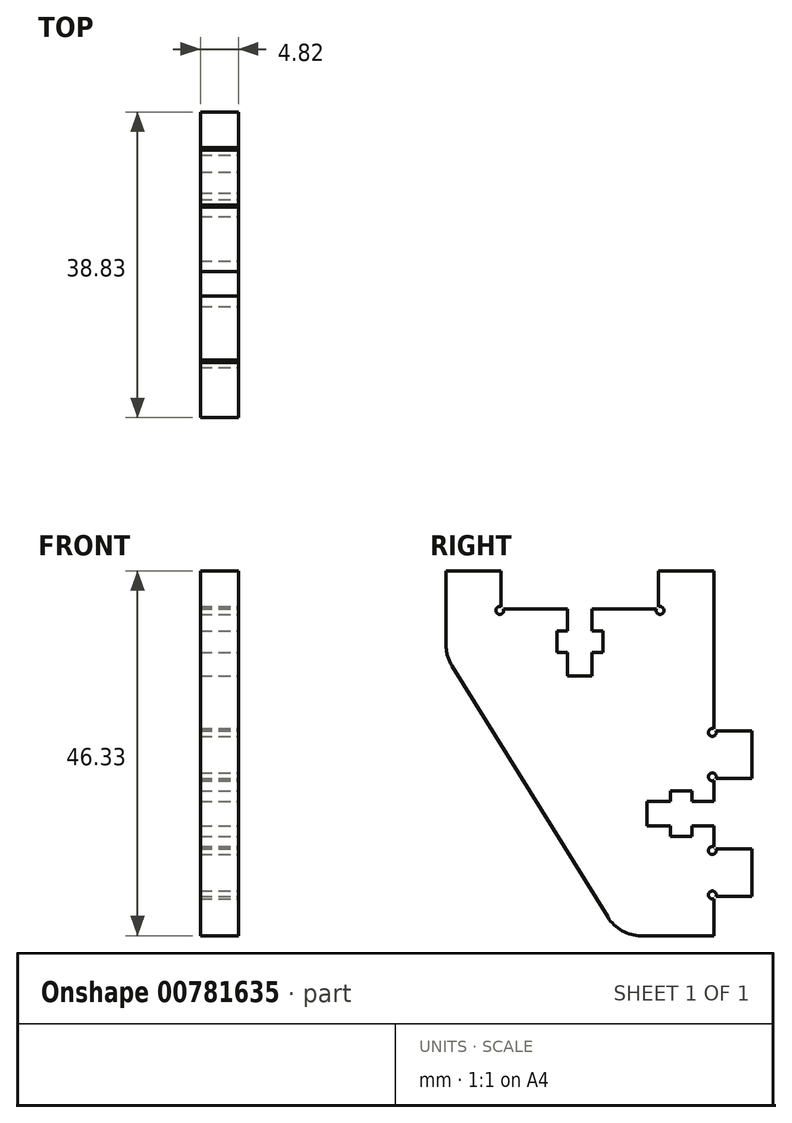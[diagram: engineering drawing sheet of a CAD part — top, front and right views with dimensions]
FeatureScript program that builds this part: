
annotation { "Feature Type Name" : "Feature", "Feature Type Description" : "" }
export const myFeature = defineFeature(function(context is Context, id is Id, definition is map)
    precondition{}
    {
        {
            var Q0;
            Q0=qCreatedBy(makeId("Right.planeOp"),FACE);
            var sketch = newSketch(context, id + "F0", { "sketchPlane" : qUnion([Q0])});
            skLineSegment(sketch, "E0.top", {"start": v(17, 0) * mm, "end": v(-17, 0) * mm});
            skLineSegment(sketch, "E0.left", {"start": v(17, -41.5) * mm, "end": v(17, 0) * mm});
            skLineSegment(sketch, "E0.right", {"start": v(-17, -6) * mm, "end": v(-17, 0) * mm});
            skPoint(sketch, "E0.middle", {"position": v(0, 0) * mm});
            skLineSegment(sketch, "E1", {"start": v(5, -41.5) * mm, "end": v(17, -41.5) * mm});
            skLineSegment(sketch, "E2", {"start": v(-17, -6) * mm, "end": v(5, -41.5) * mm});
            skSolve(sketch);
        }
        {
            var Q0;
            Q0=qSketchRegion(id+"F0",true);
            extrude(context, id + "F1", {"entities" : qUnion([Q0]), "endBound" : BoundingType.SYMMETRIC, "depth" : 4.83 * mm, "offsetDistance" : 25 * mm});
        }
        {
            var Q0;
            Q0=makeQuery(id+"FjucUZLDH5ycelK_1.boolean.opBoolean","MERGE",FACE,{"derivedFrom":[makeQuery(id+"F1.opExtrude","CAP_FACE",FACE,{"disambiguationData":[OSD([sQuery(id+"F0.wireOp",EDGE,"E0.top"),sQuery(id+"F0.wireOp",EDGE,"E0.left"),sQuery(id+"F0.wireOp",EDGE,"E0.right"),sQuery(id+"F0.wireOp",EDGE,"E1")])],"isStart":false}),makeQuery(id+"FjucUZLDH5ycelK_1.opExtrude","CAP_FACE",FACE,{"disambiguationData":[OSD([sQuery(id+"FY2jRFH9jLugM9P_1.wireOp",EDGE,"O2X1AnSx-cqAX-ZzSL-VyK4-Bfn6wNXQiSFq"),sQuery(id+"FY2jRFH9jLugM9P_1.wireOp",EDGE,"AaKU7wvq-weS6-BLke-amgP-EWbtpsUDyHzW"),sQuery(id+"FY2jRFH9jLugM9P_1.wireOp",EDGE,"irgBfRid-3kpj-Qc8P-PGbv-PMS41DCVUZRM"),sQuery(id+"FY2jRFH9jLugM9P_1.wireOp",EDGE,"iJ2sUDL7-zgiJ-5cL0-Kn1Y-U1VP3jVwUriC")])],"isStart":false}),makeQuery(id+"FjucUZLDH5ycelK_1.opExtrude","CAP_FACE",FACE,{"disambiguationData":[OSD([sQuery(id+"FY2jRFH9jLugM9P_1.wireOp",EDGE,"fd483ba7-293b-435a-8ddd-1c966510af4c0.MirrorCS"),sQuery(id+"FY2jRFH9jLugM9P_1.wireOp",EDGE,"fd483ba7-293b-435a-8ddd-1c966510af4c1.MirrorCS"),sQuery(id+"FY2jRFH9jLugM9P_1.wireOp",EDGE,"fd483ba7-293b-435a-8ddd-1c966510af4c2.MirrorCS"),sQuery(id+"FY2jRFH9jLugM9P_1.wireOp",EDGE,"fd483ba7-293b-435a-8ddd-1c966510af4c3.MirrorCS")])],"isStart":false})]});
            var sketch = newSketch(context, id + "F2", { "sketchPlane" : qUnion([Q0])});
            skLineSegment(sketch, "E3", {"start": v(8.5, -27.55) * mm, "end": v(11.5, -27.55) * mm});
            skLineSegment(sketch, "E4", {"start": v(11.5, -27.55) * mm, "end": v(11.5, -28.9) * mm});
            skLineSegment(sketch, "E5", {"start": v(11.5, -28.9) * mm, "end": v(14.2, -28.9) * mm});
            skLineSegment(sketch, "E6", {"start": v(14.2, -28.9) * mm, "end": v(14.2, -27.55) * mm});
            skLineSegment(sketch, "E7", {"start": v(14.2, -27.55) * mm, "end": v(17, -27.55) * mm});
            skLineSegment(sketch, "E8", {"start": v(17, -27.55) * mm, "end": v(17, -24.45) * mm});
            skLineSegment(sketch, "E9", {"start": v(17, -24.45) * mm, "end": v(14.2, -24.45) * mm});
            skLineSegment(sketch, "E10", {"start": v(14.2, -24.45) * mm, "end": v(14.2, -23.1) * mm});
            skLineSegment(sketch, "E11", {"start": v(14.2, -23.1) * mm, "end": v(11.5, -23.1) * mm});
            skLineSegment(sketch, "E12", {"start": v(11.5, -23.1) * mm, "end": v(11.5, -24.45) * mm});
            skLineSegment(sketch, "E13", {"start": v(11.5, -24.45) * mm, "end": v(8.5, -24.45) * mm});
            skLineSegment(sketch, "E14", {"start": v(17, -26) * mm, "end": v(8.5, -26) * mm, "construction": true});
            skLineSegment(sketch, "E15", {"start": v(8.5, -27.55) * mm, "end": v(8.5, -24.45) * mm});
            skLineSegment(sketch, "E16", {"start": v(1.55, -8.5) * mm, "end": v(1.55, -5.5) * mm});
            skLineSegment(sketch, "E17", {"start": v(1.55, -5.5) * mm, "end": v(2.9, -5.5) * mm});
            skLineSegment(sketch, "E18", {"start": v(2.9, -5.5) * mm, "end": v(2.9, -2.8) * mm});
            skLineSegment(sketch, "E19", {"start": v(2.9, -2.8) * mm, "end": v(1.55, -2.8) * mm});
            skLineSegment(sketch, "E20", {"start": v(1.55, -2.8) * mm, "end": v(1.55, 0) * mm});
            skLineSegment(sketch, "E21", {"start": v(1.55, 0) * mm, "end": v(-1.55, 0) * mm});
            skLineSegment(sketch, "E22", {"start": v(-1.55, 0) * mm, "end": v(-1.55, -2.8) * mm});
            skLineSegment(sketch, "E23", {"start": v(-1.55, -2.8) * mm, "end": v(-2.9, -2.8) * mm});
            skLineSegment(sketch, "E24", {"start": v(-2.9, -2.8) * mm, "end": v(-2.9, -5.5) * mm});
            skLineSegment(sketch, "E25", {"start": v(-2.9, -5.5) * mm, "end": v(-1.55, -5.5) * mm});
            skLineSegment(sketch, "E26", {"start": v(-1.55, -5.5) * mm, "end": v(-1.55, -8.5) * mm});
            skLineSegment(sketch, "E27", {"start": v(0, 0) * mm, "end": v(0, -8.5) * mm, "construction": true});
            skLineSegment(sketch, "E28", {"start": v(1.55, -8.5) * mm, "end": v(-1.55, -8.5) * mm});
            skSolve(sketch);
        }
        {
            var Q0;
            Q0=qSketchRegion(id+"F2",true);
            extrude(context, id + "F3", {"entities" : qUnion([Q0]), "operationType" : NewBodyOperationType.REMOVE, "endBound" : BoundingType.THROUGH_ALL, "oppositeDirection" : true, "depth" : 25 * mm, "offsetDistance" : 25 * mm});
        }
        {
            var Q0;
            Q0=makeQuery(id+"F7.boolean.opBoolean","MERGE",FACE,{"derivedFrom":[makeQuery(id+"FjucUZLDH5ycelK_1.boolean.opBoolean","MERGE",FACE,{"derivedFrom":[makeQuery(id+"F1.opExtrude","CAP_FACE",FACE,{"disambiguationData":[OSD([sQuery(id+"F0.wireOp",EDGE,"E0.top"),sQuery(id+"F0.wireOp",EDGE,"E0.left"),sQuery(id+"F0.wireOp",EDGE,"E0.right"),sQuery(id+"F0.wireOp",EDGE,"E1")])],"isStart":false}),makeQuery(id+"FjucUZLDH5ycelK_1.opExtrude","CAP_FACE",FACE,{"disambiguationData":[OSD([sQuery(id+"FY2jRFH9jLugM9P_1.wireOp",EDGE,"O2X1AnSx-cqAX-ZzSL-VyK4-Bfn6wNXQiSFq"),sQuery(id+"FY2jRFH9jLugM9P_1.wireOp",EDGE,"AaKU7wvq-weS6-BLke-amgP-EWbtpsUDyHzW"),sQuery(id+"FY2jRFH9jLugM9P_1.wireOp",EDGE,"irgBfRid-3kpj-Qc8P-PGbv-PMS41DCVUZRM"),sQuery(id+"FY2jRFH9jLugM9P_1.wireOp",EDGE,"iJ2sUDL7-zgiJ-5cL0-Kn1Y-U1VP3jVwUriC")])],"isStart":false}),makeQuery(id+"FjucUZLDH5ycelK_1.opExtrude","CAP_FACE",FACE,{"disambiguationData":[OSD([sQuery(id+"FY2jRFH9jLugM9P_1.wireOp",EDGE,"fd483ba7-293b-435a-8ddd-1c966510af4c1.MirrorCS"),sQuery(id+"FY2jRFH9jLugM9P_1.wireOp",EDGE,"fd483ba7-293b-435a-8ddd-1c966510af4c2.MirrorCS"),sQuery(id+"FY2jRFH9jLugM9P_1.wireOp",EDGE,"fd483ba7-293b-435a-8ddd-1c966510af4c3.MirrorCS"),sQuery(id+"FY2jRFH9jLugM9P_1.wireOp",EDGE,"w63aLPBc-oQ20-bgNe-LU2X-k1RGaLXDmJ6d")])],"isStart":false})]}),makeQuery(id+"F7.opExtrude","CAP_FACE",FACE,{"disambiguationData":[OSD([sQuery(id+"F6.wireOp",EDGE,"E31.bottom"),sQuery(id+"F6.wireOp",EDGE,"E31.top"),sQuery(id+"F6.wireOp",EDGE,"E31.left"),sQuery(id+"F6.wireOp",EDGE,"E31.right")])],"isStart":true})]});
            var sketch = newSketch(context, id + "F4", { "sketchPlane" : qUnion([Q0])});
            skLineSegment(sketch, "E29.bottom", {"start": v(-17, 0) * mm, "end": v(-10, 0) * mm});
            skLineSegment(sketch, "E29.top", {"start": v(-17, 4.83) * mm, "end": v(-10, 4.83) * mm});
            skLineSegment(sketch, "E29.left", {"start": v(-17, 0) * mm, "end": v(-17, 4.83) * mm});
            skLineSegment(sketch, "E29.right", {"start": v(-10, 0) * mm, "end": v(-10, 4.83) * mm});
            skLineSegment(sketch, "E30.bottom", {"start": v(17, 0) * mm, "end": v(10, 0) * mm});
            skLineSegment(sketch, "E30.top", {"start": v(17, 4.83) * mm, "end": v(10, 4.83) * mm});
            skLineSegment(sketch, "E30.left", {"start": v(17, 0) * mm, "end": v(17, 4.83) * mm});
            skLineSegment(sketch, "E30.right", {"start": v(10, 0) * mm, "end": v(10, 4.83) * mm});
            skSolve(sketch);
        }
        {
            var Q0;
            Q0=makeQuery(id+"F4.imprint","IMPRINT",FACE,{"disambiguationData":[TD([[makeQuery(id+"F4.imprint","IMPRINT",EDGE,{"derivedFrom":sQuery(id+"F4.wireOp",EDGE,"E29.bottom")}),-1.0]])]});
            var Q1;
            Q1=makeQuery(id+"F4.imprint","IMPRINT",FACE,{"disambiguationData":[TD([[makeQuery(id+"F4.imprint","IMPRINT",EDGE,{"derivedFrom":sQuery(id+"F4.wireOp",EDGE,"E30.bottom")}),-1.0]])]});
            var Q2;
            {var subQ0=sQuery(id+"FY2jRFH9jLugM9P_1.wireOp",EDGE,"w63aLPBc-oQ20-bgNe-LU2X-k1RGaLXDmJ6d");var subQ1=sQuery(id+"FY2jRFH9jLugM9P_1.wireOp",EDGE,"fd483ba7-293b-435a-8ddd-1c966510af4c3.MirrorCS");var subQ2=sQuery(id+"FY2jRFH9jLugM9P_1.wireOp",EDGE,"fd483ba7-293b-435a-8ddd-1c966510af4c2.MirrorCS");var subQ3=sQuery(id+"FY2jRFH9jLugM9P_1.wireOp",EDGE,"fd483ba7-293b-435a-8ddd-1c966510af4c1.MirrorCS");var subQ4=sQuery(id+"FY2jRFH9jLugM9P_1.wireOp",EDGE,"iJ2sUDL7-zgiJ-5cL0-Kn1Y-U1VP3jVwUriC");var subQ5=sQuery(id+"FY2jRFH9jLugM9P_1.wireOp",EDGE,"irgBfRid-3kpj-Qc8P-PGbv-PMS41DCVUZRM");var subQ6=sQuery(id+"FY2jRFH9jLugM9P_1.wireOp",EDGE,"AaKU7wvq-weS6-BLke-amgP-EWbtpsUDyHzW");var subQ7=sQuery(id+"FY2jRFH9jLugM9P_1.wireOp",EDGE,"O2X1AnSx-cqAX-ZzSL-VyK4-Bfn6wNXQiSFq");var subQ8=sQuery(id+"F0.wireOp",EDGE,"E1");var subQ9=sQuery(id+"F0.wireOp",EDGE,"E0.right");var subQ10=sQuery(id+"F0.wireOp",EDGE,"E0.left");var subQ11=sQuery(id+"F0.wireOp",EDGE,"E0.top");Q2=makeQuery(id+"F7.boolean.opBoolean","MERGE",FACE,{"derivedFrom":[makeQuery(id+"FjucUZLDH5ycelK_1.boolean.opBoolean","MERGE",FACE,{"derivedFrom":[makeQuery(id+"F1.opExtrude","CAP_FACE",FACE,{"disambiguationData":[OSD([subQ11,subQ10,subQ9,subQ8])],"isStart":true}),makeQuery(id+"FjucUZLDH5ycelK_1.opExtrude","CAP_FACE",FACE,{"disambiguationData":[OSD([subQ7,subQ6,subQ5,subQ4])],"isStart":true}),makeQuery(id+"FjucUZLDH5ycelK_1.opExtrude","CAP_FACE",FACE,{"disambiguationData":[OSD([subQ3,subQ2,subQ1,subQ0])],"isStart":true})]}),makeQuery(id+"F7.opExtrude","CAP_FACE",FACE,{"disambiguationData":[OSD([subQ11,subQ10,subQ9,subQ8,subQ7,subQ6,subQ5,subQ4,subQ3,subQ2,subQ1,subQ0])],"isStart":false})]});}
            extrude(context, id + "F5", {"entities" : qUnion([Q0, Q1]), "operationType" : NewBodyOperationType.ADD, "endBound" : BoundingType.UP_TO_SURFACE, "oppositeDirection" : true, "depth" : 25 * mm, "endBoundEntityFace" : qUnion([Q2]), "offsetDistance" : 25 * mm});
        }
        {
            var Q0;
            Q0=makeQuery(id+"FjucUZLDH5ycelK_1.boolean.opBoolean","MERGE",FACE,{"derivedFrom":[makeQuery(id+"F1.opExtrude","CAP_FACE",FACE,{"disambiguationData":[OSD([sQuery(id+"F0.wireOp",EDGE,"E0.top"),sQuery(id+"F0.wireOp",EDGE,"E0.left"),sQuery(id+"F0.wireOp",EDGE,"E0.right"),sQuery(id+"F0.wireOp",EDGE,"E1")])],"isStart":false}),makeQuery(id+"FjucUZLDH5ycelK_1.opExtrude","CAP_FACE",FACE,{"disambiguationData":[OSD([sQuery(id+"FY2jRFH9jLugM9P_1.wireOp",EDGE,"O2X1AnSx-cqAX-ZzSL-VyK4-Bfn6wNXQiSFq"),sQuery(id+"FY2jRFH9jLugM9P_1.wireOp",EDGE,"AaKU7wvq-weS6-BLke-amgP-EWbtpsUDyHzW"),sQuery(id+"FY2jRFH9jLugM9P_1.wireOp",EDGE,"irgBfRid-3kpj-Qc8P-PGbv-PMS41DCVUZRM"),sQuery(id+"FY2jRFH9jLugM9P_1.wireOp",EDGE,"iJ2sUDL7-zgiJ-5cL0-Kn1Y-U1VP3jVwUriC")])],"isStart":false}),makeQuery(id+"FjucUZLDH5ycelK_1.opExtrude","CAP_FACE",FACE,{"disambiguationData":[OSD([sQuery(id+"FY2jRFH9jLugM9P_1.wireOp",EDGE,"fd483ba7-293b-435a-8ddd-1c966510af4c1.MirrorCS"),sQuery(id+"FY2jRFH9jLugM9P_1.wireOp",EDGE,"fd483ba7-293b-435a-8ddd-1c966510af4c2.MirrorCS"),sQuery(id+"FY2jRFH9jLugM9P_1.wireOp",EDGE,"fd483ba7-293b-435a-8ddd-1c966510af4c3.MirrorCS"),sQuery(id+"FY2jRFH9jLugM9P_1.wireOp",EDGE,"w63aLPBc-oQ20-bgNe-LU2X-k1RGaLXDmJ6d")])],"isStart":false})]});
            var sketch = newSketch(context, id + "F6", { "sketchPlane" : qUnion([Q0])});
            skLineSegment(sketch, "E31.bottom", {"start": v(17, -30.5) * mm, "end": v(21.83, -30.5) * mm});
            skLineSegment(sketch, "E31.top", {"start": v(17, -36.5) * mm, "end": v(21.83, -36.5) * mm});
            skLineSegment(sketch, "E31.left", {"start": v(17, -30.5) * mm, "end": v(17, -36.5) * mm});
            skLineSegment(sketch, "E31.right", {"start": v(21.83, -30.5) * mm, "end": v(21.83, -36.5) * mm});
            skLineSegment(sketch, "E32", {"start": v(8.5, -26) * mm, "end": v(17, -26) * mm, "construction": true});
            skLineSegment(sketch, "E33", {"start": v(17, -27.55) * mm, "end": v(17, -24.45) * mm, "construction": true});
            skLineSegment(sketch, "E34.MirrorCS", {"start": v(17, -15.5) * mm, "end": v(21.83, -15.5) * mm});
            skLineSegment(sketch, "E35.MirrorCS", {"start": v(17, -21.5) * mm, "end": v(21.83, -21.5) * mm});
            skLineSegment(sketch, "E36.MirrorCS", {"start": v(17, -21.5) * mm, "end": v(17, -15.5) * mm});
            skLineSegment(sketch, "E37.MirrorCS", {"start": v(21.83, -21.5) * mm, "end": v(21.83, -15.5) * mm});
            skSolve(sketch);
        }
        {
            var Q0;
            Q0=qSketchRegion(id+"F6",true);
            var Q1;
            Q1=makeQuery(id+"FjucUZLDH5ycelK_1.boolean.opBoolean","MERGE",FACE,{"derivedFrom":[makeQuery(id+"F1.opExtrude","CAP_FACE",FACE,{"disambiguationData":[OSD([sQuery(id+"F0.wireOp",EDGE,"E0.top"),sQuery(id+"F0.wireOp",EDGE,"E0.left"),sQuery(id+"F0.wireOp",EDGE,"E0.right"),sQuery(id+"F0.wireOp",EDGE,"E1")])],"isStart":true}),makeQuery(id+"FjucUZLDH5ycelK_1.opExtrude","CAP_FACE",FACE,{"disambiguationData":[OSD([sQuery(id+"FY2jRFH9jLugM9P_1.wireOp",EDGE,"O2X1AnSx-cqAX-ZzSL-VyK4-Bfn6wNXQiSFq"),sQuery(id+"FY2jRFH9jLugM9P_1.wireOp",EDGE,"AaKU7wvq-weS6-BLke-amgP-EWbtpsUDyHzW"),sQuery(id+"FY2jRFH9jLugM9P_1.wireOp",EDGE,"irgBfRid-3kpj-Qc8P-PGbv-PMS41DCVUZRM"),sQuery(id+"FY2jRFH9jLugM9P_1.wireOp",EDGE,"iJ2sUDL7-zgiJ-5cL0-Kn1Y-U1VP3jVwUriC")])],"isStart":true}),makeQuery(id+"FjucUZLDH5ycelK_1.opExtrude","CAP_FACE",FACE,{"disambiguationData":[OSD([sQuery(id+"FY2jRFH9jLugM9P_1.wireOp",EDGE,"fd483ba7-293b-435a-8ddd-1c966510af4c1.MirrorCS"),sQuery(id+"FY2jRFH9jLugM9P_1.wireOp",EDGE,"fd483ba7-293b-435a-8ddd-1c966510af4c2.MirrorCS"),sQuery(id+"FY2jRFH9jLugM9P_1.wireOp",EDGE,"fd483ba7-293b-435a-8ddd-1c966510af4c3.MirrorCS"),sQuery(id+"FY2jRFH9jLugM9P_1.wireOp",EDGE,"w63aLPBc-oQ20-bgNe-LU2X-k1RGaLXDmJ6d")])],"isStart":true})]});
            extrude(context, id + "F7", {"entities" : qUnion([Q0]), "operationType" : NewBodyOperationType.ADD, "endBound" : BoundingType.UP_TO_SURFACE, "oppositeDirection" : true, "depth" : 25 * mm, "endBoundEntityFace" : qUnion([Q1]), "offsetDistance" : 25 * mm});
        }
        {
            var Q0;
            Q0=makeQuery(id+"F7.boolean.opBoolean","MERGE",FACE,{"derivedFrom":[makeQuery(id+"FjucUZLDH5ycelK_1.boolean.opBoolean","MERGE",FACE,{"derivedFrom":[makeQuery(id+"F1.opExtrude","CAP_FACE",FACE,{"disambiguationData":[OSD([sQuery(id+"F0.wireOp",EDGE,"E0.top"),sQuery(id+"F0.wireOp",EDGE,"E0.left"),sQuery(id+"F0.wireOp",EDGE,"E0.right"),sQuery(id+"F0.wireOp",EDGE,"E1")])],"isStart":false}),makeQuery(id+"FjucUZLDH5ycelK_1.opExtrude","CAP_FACE",FACE,{"disambiguationData":[OSD([sQuery(id+"FY2jRFH9jLugM9P_1.wireOp",EDGE,"O2X1AnSx-cqAX-ZzSL-VyK4-Bfn6wNXQiSFq"),sQuery(id+"FY2jRFH9jLugM9P_1.wireOp",EDGE,"AaKU7wvq-weS6-BLke-amgP-EWbtpsUDyHzW"),sQuery(id+"FY2jRFH9jLugM9P_1.wireOp",EDGE,"irgBfRid-3kpj-Qc8P-PGbv-PMS41DCVUZRM"),sQuery(id+"FY2jRFH9jLugM9P_1.wireOp",EDGE,"iJ2sUDL7-zgiJ-5cL0-Kn1Y-U1VP3jVwUriC")])],"isStart":false}),makeQuery(id+"FjucUZLDH5ycelK_1.opExtrude","CAP_FACE",FACE,{"disambiguationData":[OSD([sQuery(id+"FY2jRFH9jLugM9P_1.wireOp",EDGE,"fd483ba7-293b-435a-8ddd-1c966510af4c1.MirrorCS"),sQuery(id+"FY2jRFH9jLugM9P_1.wireOp",EDGE,"fd483ba7-293b-435a-8ddd-1c966510af4c2.MirrorCS"),sQuery(id+"FY2jRFH9jLugM9P_1.wireOp",EDGE,"fd483ba7-293b-435a-8ddd-1c966510af4c3.MirrorCS"),sQuery(id+"FY2jRFH9jLugM9P_1.wireOp",EDGE,"w63aLPBc-oQ20-bgNe-LU2X-k1RGaLXDmJ6d")])],"isStart":false})]}),makeQuery(id+"F7.opExtrude","CAP_FACE",FACE,{"disambiguationData":[OSD([sQuery(id+"F6.wireOp",EDGE,"E31.bottom"),sQuery(id+"F6.wireOp",EDGE,"E31.top"),sQuery(id+"F6.wireOp",EDGE,"E31.left"),sQuery(id+"F6.wireOp",EDGE,"E31.right")])],"isStart":true})]});
            var sketch = newSketch(context, id + "F8", { "sketchPlane" : qUnion([Q0])});
            skLineSegment(sketch, "E38", {"start": v(17, -36.5) * mm, "end": v(16.82, -36.32) * mm, "construction": true});
            skCircle(sketch, "E39", {"center": v(16.82, -36.32) * mm, "radius": 0.5 * mm});
            skLineSegment(sketch, "E40", {"start": v(17, -30.5) * mm, "end": v(16.82, -30.68) * mm, "construction": true});
            skCircle(sketch, "E41", {"center": v(16.82, -30.68) * mm, "radius": 0.5 * mm});
            skLineSegment(sketch, "E42", {"start": v(-10, 0) * mm, "end": v(-10.18, -0.18) * mm, "construction": true});
            skCircle(sketch, "E43", {"center": v(-10.18, -0.18) * mm, "radius": 0.5 * mm});
            skLineSegment(sketch, "E44", {"start": v(0, 0) * mm, "end": v(0, -8.5) * mm, "construction": true});
            skLineSegment(sketch, "E45.MirrorCS", {"start": v(10, 0) * mm, "end": v(10.18, -0.18) * mm, "construction": true});
            skCircle(sketch, "E46.MirrorC", {"center": v(10.18, -0.18) * mm, "radius": 0.5 * mm});
            skLineSegment(sketch, "E47", {"start": v(17, -24.45) * mm, "end": v(17, -27.55) * mm, "construction": true});
            skLineSegment(sketch, "E48", {"start": v(8.5, -26) * mm, "end": v(17, -26) * mm, "construction": true});
            skLineSegment(sketch, "E49.MirrorCS", {"start": v(17, -21.5) * mm, "end": v(16.82, -21.32) * mm, "construction": true});
            skLineSegment(sketch, "E50.MirrorCS", {"start": v(17, -15.5) * mm, "end": v(16.82, -15.68) * mm, "construction": true});
            skCircle(sketch, "E51.MirrorC", {"center": v(16.82, -15.68) * mm, "radius": 0.5 * mm});
            skCircle(sketch, "E52.MirrorC", {"center": v(16.82, -21.32) * mm, "radius": 0.5 * mm});
            skSolve(sketch);
        }
        {
            var Q0;
            Q0=qSketchRegion(id+"F8",true);
            extrude(context, id + "F9", {"entities" : qUnion([Q0]), "operationType" : NewBodyOperationType.REMOVE, "endBound" : BoundingType.THROUGH_ALL, "oppositeDirection" : true, "depth" : 25 * mm, "offsetDistance" : 25 * mm});
        }
        {
            var Q0;
            Q0=makeQuery(id+"F1.opExtrude","SWEPT_EDGE",EDGE,{"disambiguationData":[OSD([sQuery(id+"F0.wireOp",EDGE,"E0.right"),sQuery(id+"F0.wireOp",EDGE,"E2")])]});
            var Q1;
            Q1=makeQuery(id+"F1.opExtrude","SWEPT_EDGE",EDGE,{"disambiguationData":[OSD([sQuery(id+"F0.wireOp",EDGE,"E1"),sQuery(id+"F0.wireOp",EDGE,"E2")])]});
            fillet(context, id + "F10", {"entities" : qUnion([Q0, Q1]), "radius" : 5 * mm, "tangentPropagation" : true, "allowEdgeOverflow" : false});
        }
    });
